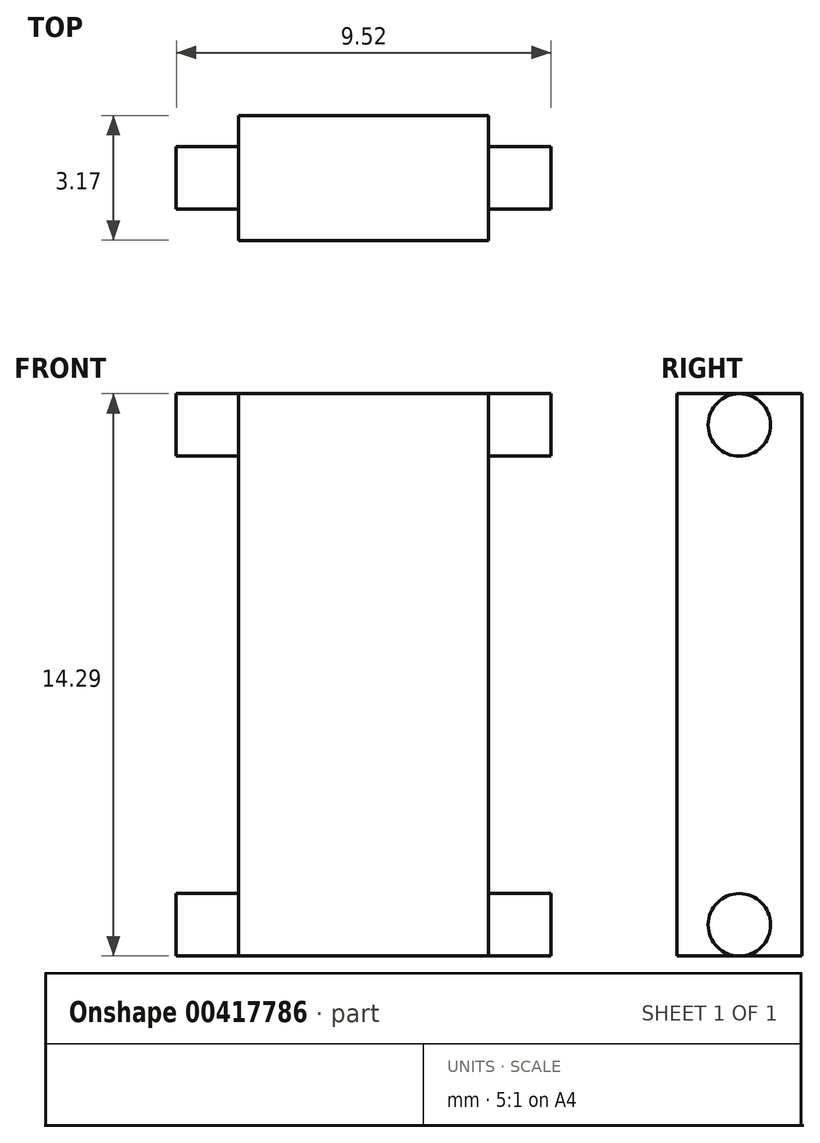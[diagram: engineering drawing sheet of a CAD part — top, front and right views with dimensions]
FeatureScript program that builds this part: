
annotation { "Feature Type Name" : "Feature", "Feature Type Description" : "" }
export const myFeature = defineFeature(function(context is Context, id is Id, definition is map)
    precondition{}
    {
        {
            var Q0;
            Q0=qCreatedBy(makeId("Front.planeOp"),FACE);
            var sketch = newSketch(context, id + "F0", { "sketchPlane" : qUnion([Q0])});
            skLineSegment(sketch, "E0.bottom", {"start": v(-36.28, 19.66) * mm, "end": v(-42.63, 19.66) * mm});
            skLineSegment(sketch, "E0.top", {"start": v(-36.28, 32.36) * mm, "end": v(-42.63, 32.36) * mm});
            skLineSegment(sketch, "E0.left", {"start": v(-36.28, 19.66) * mm, "end": v(-36.28, 32.36) * mm});
            skLineSegment(sketch, "E0.right", {"start": v(-42.63, 19.66) * mm, "end": v(-42.63, 32.36) * mm});
            skPoint(sketch, "E0.middle", {"position": v(-39.45, 26.01) * mm});
            skSolve(sketch);
        }
        {
            var Q0;
            Q0=makeQuery(id+"F0.imprint","IMPRINT",FACE,{"disambiguationData":[TD([[makeQuery(id+"F0.imprint","IMPRINT",EDGE,{"derivedFrom":sQuery(id+"F0.wireOp",EDGE,"E0.bottom")}),-1.0]])]});
            extrude(context, id + "F1", {"entities" : qUnion([Q0]), "depth" : 3.17 * mm});
        }
        {
            var Q0;
            Q0=makeQuery(id+"F1.opExtrude","SWEPT_FACE",FACE,{"disambiguationData":[OSD([sQuery(id+"F0.wireOp",EDGE,"E0.bottom")])]});
            extrude(context, id + "F2", {"entities" : qUnion([Q0]), "operationType" : NewBodyOperationType.ADD, "depth" : 0.8 * mm});
        }
        {
            var Q0;
            Q0=makeQuery(id+"F1.opExtrude","SWEPT_FACE",FACE,{"disambiguationData":[OSD([sQuery(id+"F0.wireOp",EDGE,"E0.top")])]});
            extrude(context, id + "F3", {"entities" : qUnion([Q0]), "operationType" : NewBodyOperationType.ADD, "depth" : 0.8 * mm});
        }
        {
            var Q0;
            {var subQ0=sQuery(id+"F0.wireOp",EDGE,"E0.right");Q0=makeQuery(id+"F3.boolean.opBoolean","MERGE",FACE,{"derivedFrom":[makeQuery(id+"F2.boolean.opBoolean","MERGE",FACE,{"derivedFrom":[makeQuery(id+"F1.opExtrude","SWEPT_FACE",FACE,{"disambiguationData":[OSD([subQ0])]}),makeQuery(id+"F2.opExtrude","SWEPT_FACE",FACE,{"disambiguationData":[OSD([sQuery(id+"F0.wireOp",EDGE,"E0.bottom"),subQ0])]})]}),makeQuery(id+"F3.opExtrude","SWEPT_FACE",FACE,{"disambiguationData":[OSD([sQuery(id+"F0.wireOp",EDGE,"E0.top"),subQ0])]})]});}
            var sketch = newSketch(context, id + "F4", { "sketchPlane" : qUnion([Q0])});
            skCircle(sketch, "E1", {"center": v(1.59, 32.36) * mm, "radius": 0.8 * mm});
            skCircle(sketch, "E2", {"center": v(1.59, 19.66) * mm, "radius": 0.8 * mm});
            skSolve(sketch);
        }
        {
            var Q0;
            Q0=makeQuery(id+"F4.imprint","IMPRINT",FACE,{"disambiguationData":[TD([[makeQuery(id+"F4.imprint","IMPRINT",EDGE,{"derivedFrom":sQuery(id+"F4.wireOp",EDGE,"E1")}),1.0]])]});
            var Q1;
            Q1=makeQuery(id+"F4.imprint","IMPRINT",FACE,{"disambiguationData":[TD([[makeQuery(id+"F4.imprint","IMPRINT",EDGE,{"derivedFrom":sQuery(id+"F4.wireOp",EDGE,"E2")}),1.0]])]});
            var Q2;
            {var subQ0=sQuery(id+"F0.wireOp",EDGE,"E0.left");Q2=makeQuery(id+"F3.boolean.opBoolean","MERGE",FACE,{"derivedFrom":[makeQuery(id+"F2.boolean.opBoolean","MERGE",FACE,{"derivedFrom":[makeQuery(id+"F1.opExtrude","SWEPT_FACE",FACE,{"disambiguationData":[OSD([subQ0])]}),makeQuery(id+"F2.opExtrude","SWEPT_FACE",FACE,{"disambiguationData":[OSD([sQuery(id+"F0.wireOp",EDGE,"E0.bottom"),subQ0])]})]}),makeQuery(id+"F3.opExtrude","SWEPT_FACE",FACE,{"disambiguationData":[OSD([sQuery(id+"F0.wireOp",EDGE,"E0.top"),subQ0])]})]});}
            extrude(context, id + "F5", {"entities" : qUnion([Q0, Q1]), "operationType" : NewBodyOperationType.ADD, "endBoundEntityFace" : qUnion([Q2]), "depth" : 1.59 * mm});
        }
        {
            var Q0;
            {var subQ0=sQuery(id+"F0.wireOp",EDGE,"E0.left");Q0=makeQuery(id+"F3.boolean.opBoolean","MERGE",FACE,{"derivedFrom":[makeQuery(id+"F2.boolean.opBoolean","MERGE",FACE,{"derivedFrom":[makeQuery(id+"F1.opExtrude","SWEPT_FACE",FACE,{"disambiguationData":[OSD([subQ0])]}),makeQuery(id+"F2.opExtrude","SWEPT_FACE",FACE,{"disambiguationData":[OSD([sQuery(id+"F0.wireOp",EDGE,"E0.bottom"),subQ0])]})]}),makeQuery(id+"F3.opExtrude","SWEPT_FACE",FACE,{"disambiguationData":[OSD([sQuery(id+"F0.wireOp",EDGE,"E0.top"),subQ0])]})]});}
            var sketch = newSketch(context, id + "F6", { "sketchPlane" : qUnion([Q0])});
            skPoint(sketch, "E3.endSnap0", {"position": v(-1.59, 18.87) * mm});
            skCircle(sketch, "E4", {"center": v(-1.59, 32.36) * mm, "radius": 0.8 * mm});
            skCircle(sketch, "E5", {"center": v(-1.59, 19.66) * mm, "radius": 0.8 * mm});
            skSolve(sketch);
        }
        {
            var Q0;
            Q0=makeQuery(id+"F6.imprint","IMPRINT",FACE,{"disambiguationData":[TD([[makeQuery(id+"F6.imprint","IMPRINT",EDGE,{"derivedFrom":sQuery(id+"F6.wireOp",EDGE,"E4")}),1.0]])]});
            var Q1;
            Q1=makeQuery(id+"F6.imprint","IMPRINT",FACE,{"disambiguationData":[TD([[makeQuery(id+"F6.imprint","IMPRINT",EDGE,{"derivedFrom":sQuery(id+"F6.wireOp",EDGE,"E5")}),1.0]])]});
            extrude(context, id + "F7", {"entities" : qUnion([Q0, Q1]), "operationType" : NewBodyOperationType.ADD, "depth" : 1.59 * mm});
        }
    });
